# Revit family: CHUR104 Chartham Exposed Urinal Rev00 - Copy
name_source: partatom
category: Generic Models
revit_build: Autodesk Revit 2015 (Build: 20140606_1530(x64)
units: mm (PartAtom-declared; Revit-internal decimal feet)

## types (1)
- SWC_WC_CHUR104
    Brand = SanCeram
    Help = http://www.theswc.co.uk
    Manufacturer URL = www.theswc.co.uk
    NBS Reference Code = N13 - 300
    NBS Reference Description = URINALS & AUTO FLUSHING VALVES
    Name = Chartham exposed trap urinal
    Nominal Height = 445 mm
    Nominal Length = 330 mm
    Nominal Width = 355 mm
    Primary Finishes = Alpine White
    Primary Material = Vitreous China
    Product Family = Sanitary
    Product Group = Wall hung urinals
    Product Information = http://www.theswc.co.uk
    Product SKU = CHUR104
    Spare Parts = http://www.theswc.co.uk
    Trap = Exposed trap
    Urinal Mounting = Wall Mounted
    Urinal Type = Bowl
    Weight = 10 kg

## geometry (parser evidence)
native form markers: Blend x2, Sweep x2
no freeform markers — native parametric forms only
